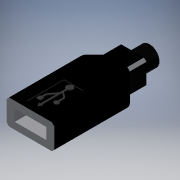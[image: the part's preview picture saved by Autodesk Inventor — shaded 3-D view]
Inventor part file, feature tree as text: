
AUTODESK INVENTOR PART (.ipt)
format: ipt  version: 2018 (Build 220112000, 112)  size: 336,384 bytes
history: native  units: mm
features: sketch x8, extrude x6, fillet x3, chamfer x2, plane x1
ambient origin geometry x8: Origin, YZ Plane, XZ Plane, XY Plane, X Axis, Y Axis, Z Axis, Center Point
bodies: Solid1 (feature_tree)
feature tree (20):
  extrude  "Extrusion1"  Depth=30.0mm
  chamfer  "Chamfer1"  Distance=10.0mm
  fillet  "Fillet1"  Radius=0.5mm
  fillet  "Fillet2"  Radius=3.0mm
  fillet  "Fillet3"  Radius=3.0mm
  extrude  "Extrusion2"  Depth=14.9mm
  extrude  "Extrusion7"  Depth=0.3mm TaperAngle=0.0deg
  plane  "Work Plane1"
  extrude  "Extrusion14"  Depth=12.5mm
  sketch  "Sketch18"  dims[d14=7.75mm d15=14.9mm]
  sketch  "Sketch19"  dims[d16=2.3mm d17=0.3mm d18=0.0mm]
  extrude  "Extrusion15"  Depth=6.75mm TaperAngle=0.0deg
  chamfer  "Chamfer2"  Distance=2.26mm
  extrude  "Extrusion16"  Depth=11.04mm
  sketch  "Sketch1"  dims[d2=19.05mm d3=30.0mm]
  sketch  "Sketch2"  dims[d4=11.04mm]
  sketch  "Sketch8"  dims[d5=4.0mm d6=10.0mm d7=0.0mm]
  sketch  "Sketch17"  dims[d8=1.0mm d9=2.0mm d10=45.0deg d11=0.5mm d12=3.0mm d13=3.0mm]
  sketch  "Sketch20"  dims[d71=0.3mm d72=0.0mm d101=12.5mm]
  sketch  "Sketch21"  dims[d102=4.52mm d106=20.0mm d107=0.0mm d108=2.26mm d109=11.04mm d110=6.6mm d111=0.0mm d112=1.0mm d113=2.0mm d114=45.0deg d115=7.9mm d116=6.75mm d117=0.0mm]
